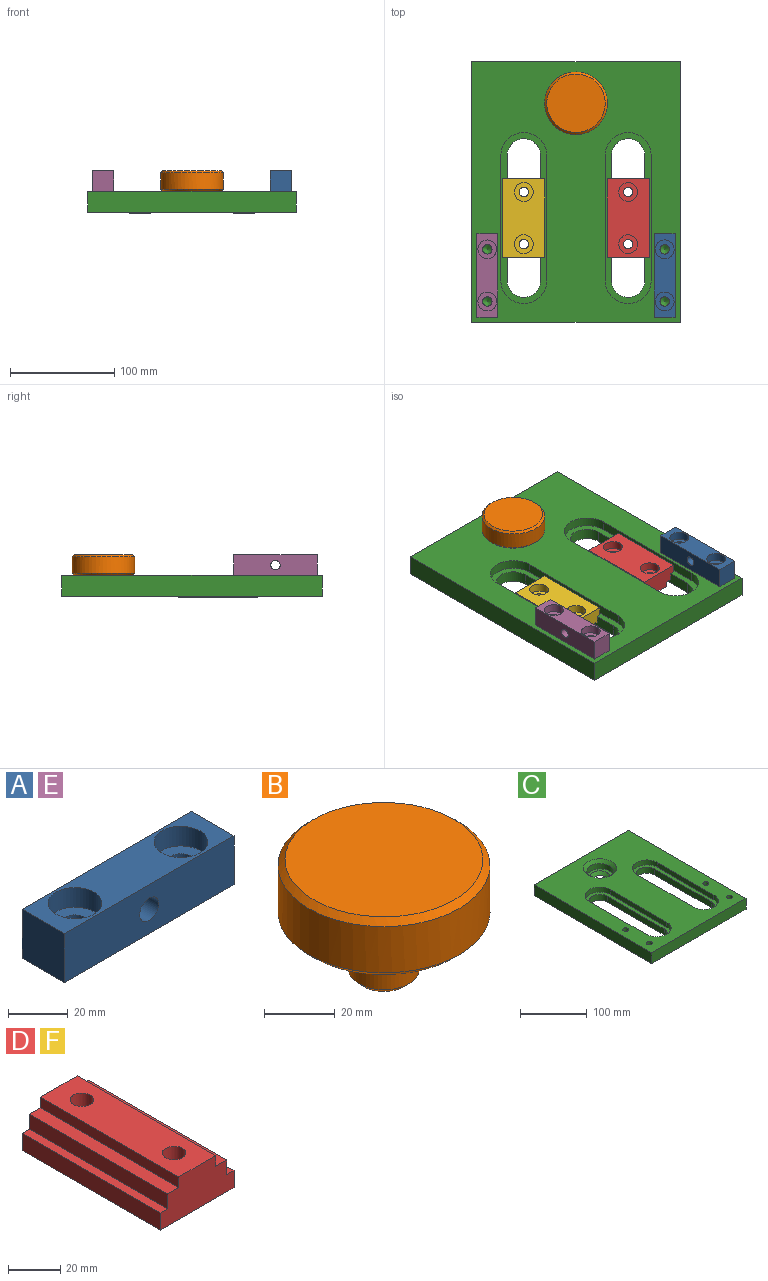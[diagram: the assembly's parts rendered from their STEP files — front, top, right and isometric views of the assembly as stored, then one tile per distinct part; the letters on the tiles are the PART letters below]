
ASSEMBLY  parts=6 mates=13
PART A: 13 faces, bbox 80x20x20 mm
  f0: plane 20x20mm, normal (1,0,0), area 400mm2, adj f1,f3,f4,f5
  f1: plane 80x20mm, normal (0,0,1), area 1091.1mm2, adj f0,f2,f4,f5,f9,f12
  f2: plane 20x20mm, normal (-1,0,0), area 400mm2, adj f1,f3,f4,f5
  f3: plane 80x20mm, normal (0,0,-1), area 1472.8mm2, adj f0,f2,f4,f5,f7,f10
  f4: plane 80x20mm, normal (0,-1,0), area 1536.4mm2, adj f0,f1,f2,f3,f6
  f5: plane 80x20mm, normal (0,1,0), area 1536.4mm2, adj f0,f1,f2,f3,f6
  f6: cylinder r=4.5mm len=20mm, axis (0,-1,0), area 565.5mm2, adj f4,f5
  f7: cylinder r=4.5mm len=12mm, axis (0,0,1), area 339.3mm2, adj f3,f8
  f8: plane 18x18mm, normal (0,0,1), area 190.9mm2, adj f7,f9
  f9: cylinder r=9mm len=18mm, axis (0,0,1), area 452.4mm2, adj f1,f8
  f10: cylinder r=4.5mm len=12mm, axis (0,0,1), area 339.3mm2, adj f3,f11
  f11: plane 18x18mm, normal (0,0,1), area 190.9mm2, adj f10,f12
  f12: cylinder r=9mm len=18mm, axis (0,0,1), area 452.4mm2, adj f1,f11
PART B: 9 faces, bbox 60x60x40 mm
  f0: plane 16x16mm, normal (0,0,-1), area 201.1mm2, adj f5
  f1: cylinder r=10mm len=20mm, axis (0,0,-1), area 1005.3mm2, adj f5,f6
  f2: plane 56x56mm, normal (0,0,-1), area 2010.6mm2, adj f6,f7
  f3: cylinder r=30mm len=60mm, axis (0,0,-1), area 3015.9mm2, adj f7,f8
  f4: plane 56x56mm, normal (0,0,1), area 2463mm2, adj f8
  f5: cone r=8mm half-angle=45deg, axis (0,0,1), area 159.9mm2, adj f0,f1
  f6: cone r=10mm half-angle=45deg, axis (0,0,1), area 195.5mm2, adj f1,f2
  f7: cone r=28mm half-angle=45deg, axis (0,0,1), area 515.4mm2, adj f2,f3
  f8: cone r=30mm half-angle=45deg, axis (0,0,-1), area 515.4mm2, adj f3,f4
PART C: 36 faces, bbox 200x250x20 mm
  f0: cylinder r=16mm len=32mm, axis (0,0,-1), area 552.9mm2, adj f1,f7,f13,f14
  f1: plane 120x11mm, normal (-1,0,0), area 1320mm2, adj f0,f2,f13,f14
  f2: cylinder r=16mm len=32mm, axis (0,0,-1), area 552.9mm2, adj f1,f7,f13,f14
  f3: plane 120x11mm, normal (1,0,0), area 1320mm2, adj f4,f6,f13,f23
  f4: cylinder r=16mm len=32mm, axis (0,0,-1), area 552.9mm2, adj f3,f5,f13,f23
  f5: plane 120x11mm, normal (-1,0,0), area 1320mm2, adj f4,f6,f13,f23
  f6: cylinder r=16mm len=32mm, axis (0,0,-1), area 552.9mm2, adj f3,f5,f13,f23
  f7: plane 120x11mm, normal (1,0,0), area 1320mm2, adj f0,f2,f13,f14
  f8: plane 250x200mm, normal (0,0,1), area 34181mm2, adj f9,f10,f11,f12,f15,f16,f17,f18
  f9: plane 250x20mm, normal (1,0,0), area 5000mm2, adj f8,f10,f12,f13
  f10: plane 200x20mm, normal (0,1,0), area 4000mm2, adj f8,f9,f11,f13
  f11: plane 250x20mm, normal (-1,0,0), area 5000mm2, adj f8,f10,f12,f13
  f12: plane 200x20mm, normal (0,-1,0), area 4000mm2, adj f8,f9,f11,f13
  f13: plane 250x200mm, normal (0,0,-1), area 40397.3mm2, adj f0,f1,f2,f3,f4,f5,f6,f7
  f14: plane 164x44mm, normal (0,0,1), area 2156.3mm2, adj f0,f1,f2,f7,f15,f16,f17,f18
  f15: plane 120x9mm, normal (-1,0,0), area 1080mm2, adj f8,f14,f16,f18
  f16: cylinder r=22mm len=44mm, axis (0,0,1), area 622mm2, adj f8,f14,f15,f17
  f17: plane 120x9mm, normal (1,0,0), area 1080mm2, adj f8,f14,f16,f18
  f18: cylinder r=22mm len=44mm, axis (0,0,1), area 622mm2, adj f8,f14,f15,f17
  f19: cylinder r=22mm len=44mm, axis (0,0,1), area 622mm2, adj f8,f20,f22,f23
  f20: plane 120x9mm, normal (1,0,0), area 1080mm2, adj f8,f19,f21,f23
  f21: cylinder r=22mm len=44mm, axis (0,0,1), area 622mm2, adj f8,f20,f22,f23
  f22: plane 120x9mm, normal (-1,0,0), area 1080mm2, adj f8,f19,f21,f23
  f23: plane 164x44mm, normal (0,0,1), area 2156.3mm2, adj f3,f4,f5,f6,f19,f20,f21,f22
  f24: plane 40x40mm, normal (0,0,1), area 549.8mm2, adj f25,f34
  f25: cylinder r=20mm len=40mm, axis (0,0,1), area 1256.6mm2, adj f24,f35
  f26: cone r=0mm half-angle=59deg, axis (0,0,1), area 74.2mm2, adj f27
  f27: cylinder r=4.5mm len=16mm, axis (0,0,1), area 452.4mm2, adj f8,f26
  f28: cone r=0mm half-angle=59deg, axis (0,0,1), area 74.2mm2, adj f29
  f29: cylinder r=4.5mm len=16mm, axis (0,0,1), area 452.4mm2, adj f8,f28
  f30: cone r=0mm half-angle=59deg, axis (0,0,1), area 74.2mm2, adj f31
  f31: cylinder r=4.5mm len=16mm, axis (0,0,1), area 452.4mm2, adj f8,f30
  f32: cone r=0mm half-angle=59deg, axis (0,0,1), area 74.2mm2, adj f33
  f33: cylinder r=4.5mm len=16mm, axis (0,0,1), area 452.4mm2, adj f8,f32
  f34: cone r=10mm half-angle=45deg, axis (0,0,1), area 555.4mm2, adj f13,f24
  f35: cone r=20mm half-angle=45deg, axis (0,0,1), area 999.6mm2, adj f8,f25
PART D: 20 faces, bbox 40x75x20 mm
  f0: plane 75x40mm, normal (0,0,-1), area 2491.1mm2, adj f1,f11,f12,f13,f16,f19
  f1: plane 75x8mm, normal (1,0,0), area 600mm2, adj f0,f2,f12,f13
  f2: plane 75x4mm, normal (0,0,1), area 300mm2, adj f1,f3,f12,f13
  f3: plane 75x7mm, normal (1,0,0), area 525mm2, adj f2,f4,f12,f13
  f4: plane 75x6mm, normal (0,0,1), area 450mm2, adj f3,f5,f12,f13
  f5: plane 75x5mm, normal (1,0,0), area 375mm2, adj f4,f6,f12,f13
  f6: plane 75x20mm, normal (0,0,1), area 1372.8mm2, adj f5,f7,f12,f13,f14,f17
  f7: plane 75x5mm, normal (-1,0,0), area 375mm2, adj f6,f8,f12,f13
  f8: plane 75x6mm, normal (0,0,1), area 450mm2, adj f7,f9,f12,f13
  f9: plane 75x7mm, normal (-1,0,0), area 525mm2, adj f8,f10,f12,f13
  f10: plane 75x4mm, normal (0,0,1), area 300mm2, adj f9,f11,f12,f13
  f11: plane 75x8mm, normal (-1,0,0), area 600mm2, adj f0,f10,f12,f13
  f12: plane 40x20mm, normal (0,-1,0), area 644mm2, adj f0,f1,f2,f3,f4,f5,f6,f7
  f13: plane 40x20mm, normal (0,1,0), area 644mm2, adj f0,f1,f2,f3,f4,f5,f6,f7
  f14: cylinder r=4.5mm len=12mm, axis (0,0,-1), area 339.3mm2, adj f6,f15
  f15: plane 18x18mm, normal (0,0,-1), area 190.9mm2, adj f14,f16
  f16: cylinder r=9mm len=18mm, axis (0,0,-1), area 452.4mm2, adj f0,f15
  f17: cylinder r=4.5mm len=12mm, axis (0,0,-1), area 339.3mm2, adj f6,f18
  f18: plane 18x18mm, normal (0,0,-1), area 190.9mm2, adj f17,f19
  f19: cylinder r=9mm len=18mm, axis (0,0,-1), area 452.4mm2, adj f0,f18
PART E: same geometry as A
PART F: same geometry as D
PLACE A rot(axis=(0,0,-1),90deg) t=(85,-83.6,10)mm
PLACE B t=(0,81.4,-20)mm
PLACE C t=(0,-3.6,-20)mm fixed
PLACE D rot(axis=(1,0,0),180deg) t=(50,-28.6,-1)mm
PLACE E rot(axis=(0,0,1),90deg) t=(-85,-83.6,10)mm
PLACE F rot(axis=(1,0,0),180deg) t=(-50,-28.6,-1)mm
MATE planar E.f3 <-> C.f8  axis (0,0,-1) through (-85,-83.6,0)mm
MATE cylindrical A.f10 <-> C.f32  axis (0,0,1) through (85,-58.6,12)mm
MATE cylindrical E.f10 <-> C.f28  axis (0,0,1) through (-85,-108.6,12)mm
MATE planar F.f12 <-> D.f12  axis (0,1,0) through (-50,8.9,-9.7)mm
MATE planar C.f8 <-> A.f3  axis (0,0,1) through (100,121.4,0)mm
MATE slider B.f1 <-> C.f25  axis (0,0,-1) through (0,81.4,-10)mm
MATE planar D.f3 <-> C.f1  axis (1,0,0) through (66,-28.6,-12.5)mm
MATE planar B.f1 <-> C.f8  axis (0,0,-1) through (0,81.4,0)mm
MATE planar F.f10 <-> C.f23  axis (0,0,-1) through (-68,-28.6,-9)mm
MATE planar D.f2 <-> C.f14  axis (0,0,-1) through (66,8.9,-9)mm
MATE cylindrical A.f7 <-> C.f30  axis (0,0,1) through (85,-108.6,6)mm
MATE planar F.f9 <-> C.f3  axis (-1,0,0) through (-66,-28.6,-12.5)mm
MATE cylindrical E.f7 <-> C.f26  axis (0,0,1) through (-85,-58.6,12)mm
